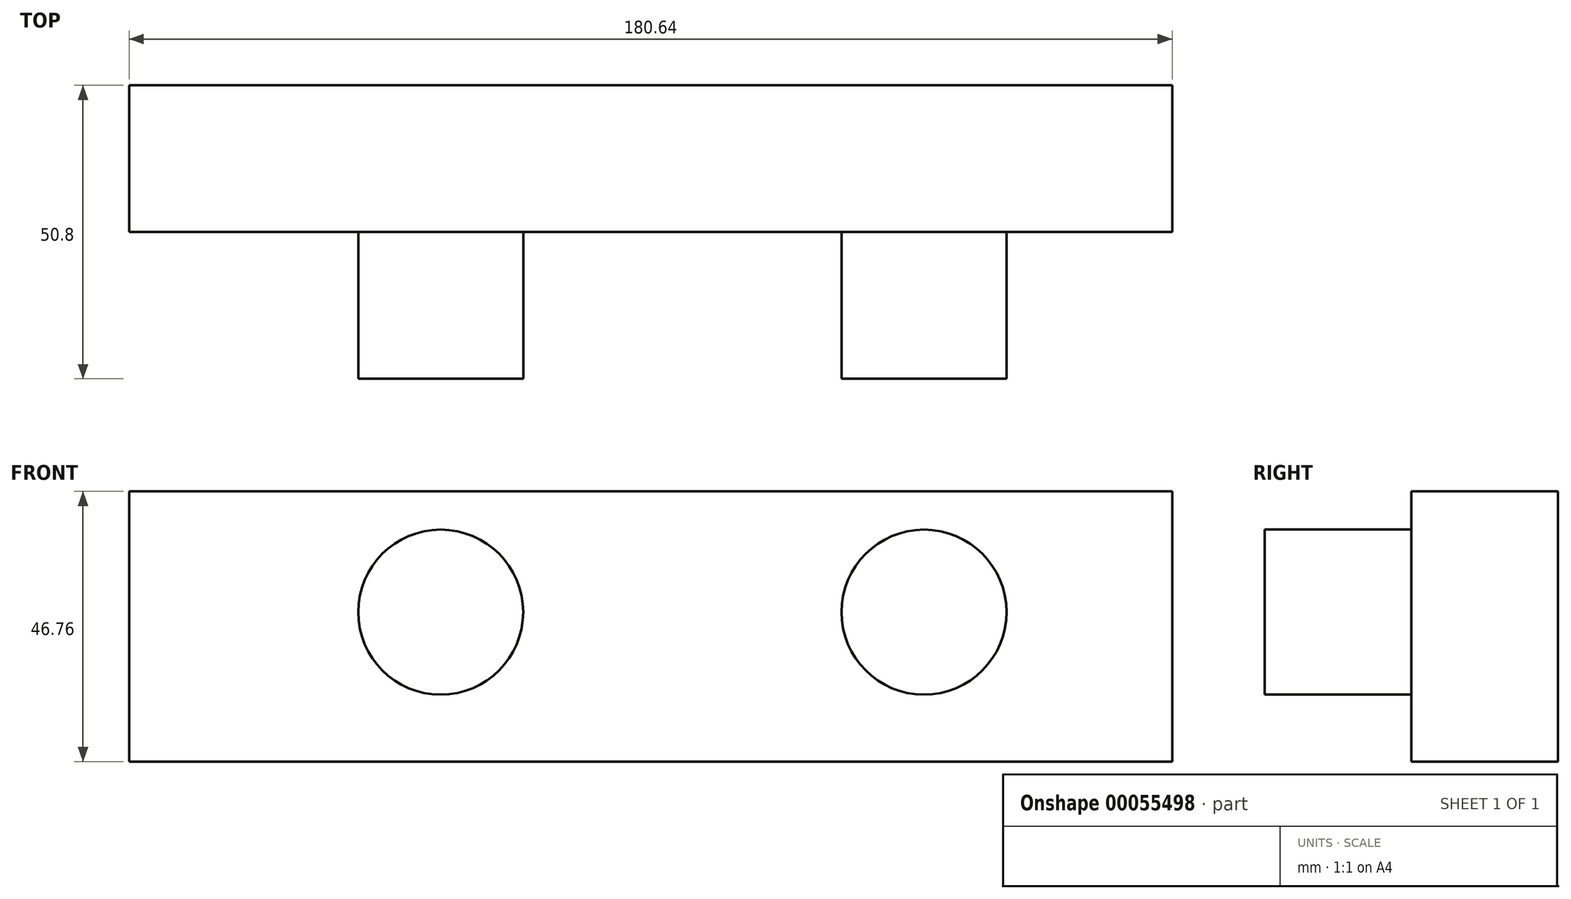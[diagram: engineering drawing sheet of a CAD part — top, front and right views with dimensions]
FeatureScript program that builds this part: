
annotation { "Feature Type Name" : "Feature", "Feature Type Description" : "" }
export const myFeature = defineFeature(function(context is Context, id is Id, definition is map)
    precondition{}
    {
        {
            var Q0;
            Q0=qCreatedBy(makeId("Front.planeOp"),FACE);
            var sketch = newSketch(context, id + "F0", { "sketchPlane" : qUnion([Q0])});
            skLineSegment(sketch, "E0.bottom", {"start": v(-46.76, 45.62) * mm, "end": v(86.65, 45.62) * mm});
            skLineSegment(sketch, "E0.top", {"start": v(-46.76, 0) * mm, "end": v(86.65, 0) * mm});
            skLineSegment(sketch, "E0.left", {"start": v(-46.76, 45.62) * mm, "end": v(-46.76, 0) * mm});
            skLineSegment(sketch, "E0.right", {"start": v(86.65, 45.62) * mm, "end": v(86.65, 0) * mm});
            skCircle(sketch, "E1", {"center": v(-19.62, 22.8) * mm, "radius": 14.29 * mm});
            skCircle(sketch, "E2", {"center": v(64.1, 22.8) * mm, "radius": 14.29 * mm});
            skPoint(sketch, "E3.orphan", {"position": v(19.95, 45.62) * mm});
            skPoint(sketch, "E4.start.orphan", {"position": v(19.95, 0) * mm});
            skPoint(sketch, "E5.orphan", {"position": v(-46.76, 22.8) * mm});
            skPoint(sketch, "E6.trimOffspring.end.orphan", {"position": v(86.65, 22.8) * mm});
            skSolve(sketch);
        }
        {
            var Q0;
            Q0=makeQuery(id+"F0.imprint","IMPRINT",FACE,{"disambiguationData":[TD([[makeQuery(id+"F0.imprint","IMPRINT",EDGE,{"derivedFrom":sQuery(id+"F0.wireOp",EDGE,"E1")}),1.0]])]});
            var Q1;
            Q1=makeQuery(id+"F0.imprint","IMPRINT",FACE,{"disambiguationData":[TD([[makeQuery(id+"F0.imprint","IMPRINT",EDGE,{"derivedFrom":sQuery(id+"F0.wireOp",EDGE,"E2")}),1.0]])]});
            extrude(context, id + "F1", {"entities" : qUnion([Q0, Q1]), "depth" : 25.4 * mm});
        }
        {
            var Q0;
            Q0=qCreatedBy(makeId("Front.planeOp"),FACE);
            var sketch = newSketch(context, id + "F2", { "sketchPlane" : qUnion([Q0])});
            skLineSegment(sketch, "E7.bottom", {"start": v(107.07, 43.7) * mm, "end": v(-73.57, 43.7) * mm});
            skLineSegment(sketch, "E7.top", {"start": v(107.07, -3.05) * mm, "end": v(-73.57, -3.05) * mm});
            skLineSegment(sketch, "E7.left", {"start": v(107.07, 43.7) * mm, "end": v(107.07, -3.05) * mm});
            skLineSegment(sketch, "E7.right", {"start": v(-73.57, 43.7) * mm, "end": v(-73.57, -3.05) * mm});
            skSolve(sketch);
        }
        {
            var Q0;
            Q0=makeQuery(id+"F2.imprint","IMPRINT",FACE,{"disambiguationData":[TD([[makeQuery(id+"F2.imprint","IMPRINT",EDGE,{"derivedFrom":sQuery(id+"F2.wireOp",EDGE,"E7.bottom")}),1.0]])]});
            extrude(context, id + "F3", {"entities" : qUnion([Q0]), "oppositeDirection" : true, "depth" : 25.4 * mm});
        }
    });
